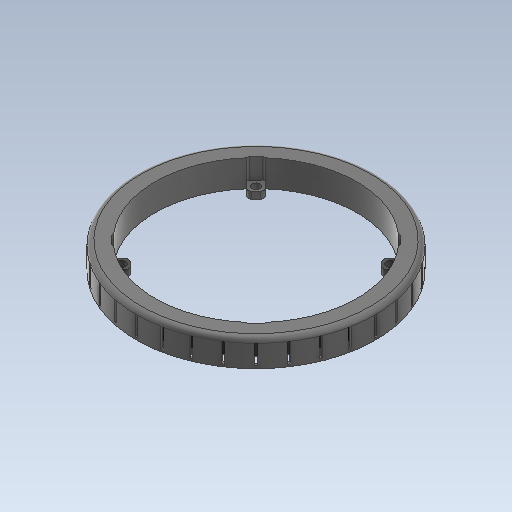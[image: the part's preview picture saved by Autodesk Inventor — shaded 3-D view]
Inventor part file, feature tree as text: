
AUTODESK INVENTOR PART (.ipt)
format: ipt  version: 2020 (Build 240168000, 168)  size: 915,456 bytes
history: native  units: mm
features: extrude x7, projected_geometry x7, sketch x6, pattern_circular x4, fillet x3, other x1
ambient origin geometry x8: Origin, YZ Plane, XZ Plane, XY Plane, X Axis, Y Axis, Z Axis, Center Point
bodies: Body1 (feature_tree)
feature tree (28):
  other  "Твердое тело1"
  sketch  "Эскиз1"
  extrude  "Выдавливание1"  Depth=88.0mm
  extrude  "Выдавливание2"  Depth=5.3mm
  pattern_circular  "Круговой массив1"  [2 undecoded]
  extrude  "Выдавливание3"  Depth=5.1mm
  fillet  "Сопряжение1"  Radius=98.0mm
  extrude  "Выдавливание4"  Depth=84.0mm
  pattern_circular  "Круговой массив2"  [2 undecoded]
  fillet  "Сопряжение2"  Radius=98.0mm
  extrude  "Выдавливание5"  Depth=84.0mm
  pattern_circular  "Круговой массив3"  [2 undecoded]
  extrude  "Выдавливание6"  Depth=10.0mm TaperAngle=0.0deg
  fillet  "Сопряжение3"  Radius=320.0mm
  sketch  "Эскиз6"
  extrude  "Выдавливание7"  Depth=2.0mm
  pattern_circular  "Круговой массив4"  [2 undecoded]
  sketch  "Эскиз2"
  sketch  "Эскиз3"
  projected_geometry  "Спроецированная петля1"
  sketch  "Эскиз4"
  projected_geometry  "Спроецированная петля2"
  sketch  "Эскиз5"
  projected_geometry  "Спроецированная петля3"
  projected_geometry  "Спроецированная петля4"
  projected_geometry  "Спроецированная петля5"
  projected_geometry  "Спроецированная петля6"
  projected_geometry  "Спроецированная петля7"
note: 8 required parameter values undecoded (feature->parameter linkage not recoverable at this tier; creation-order binding heuristic only, values carry confidence <= 0.55)
